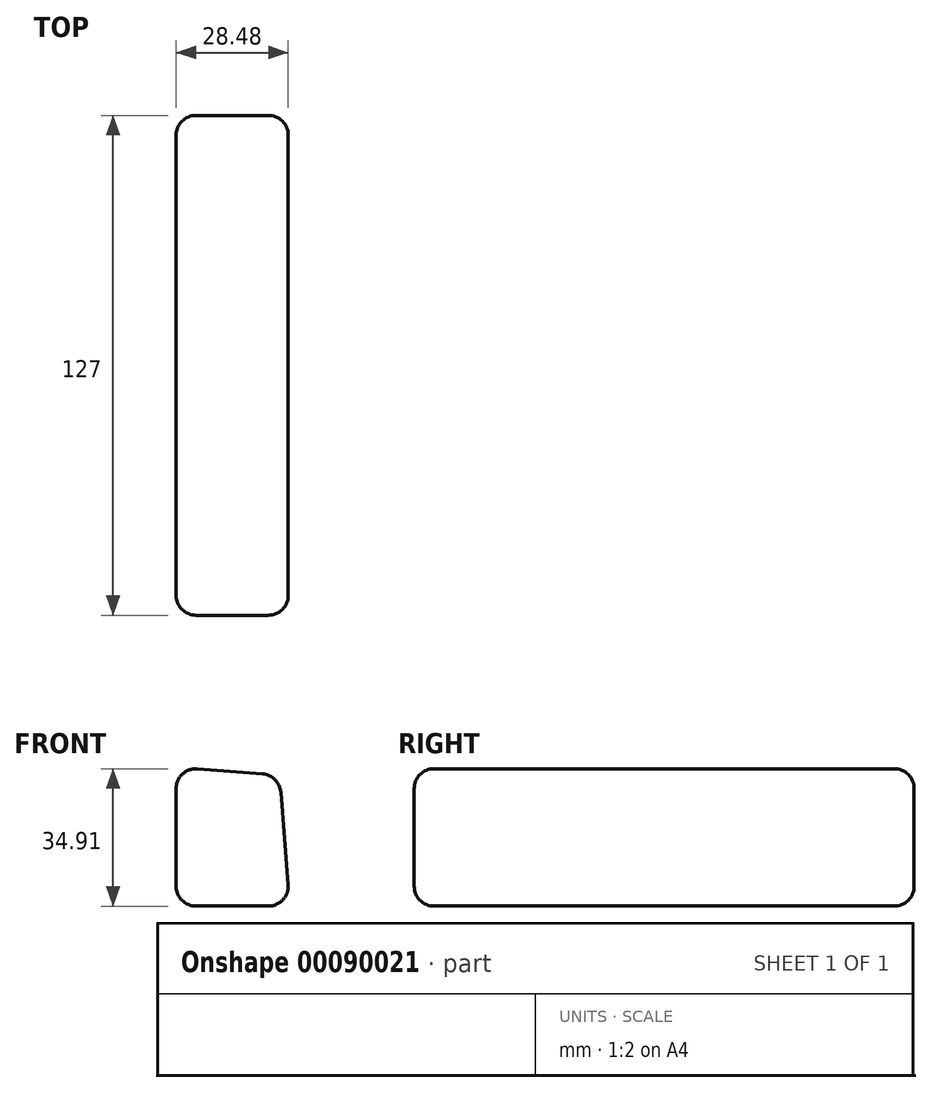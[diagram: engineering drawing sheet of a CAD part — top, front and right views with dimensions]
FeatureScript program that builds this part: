
annotation { "Feature Type Name" : "Feature", "Feature Type Description" : "" }
export const myFeature = defineFeature(function(context is Context, id is Id, definition is map)
    precondition{}
    {
        {
            var Q0;
            Q0=qCreatedBy(makeId("Front.planeOp"),FACE);
            var sketch = newSketch(context, id + "F0", { "sketchPlane" : qUnion([Q0])});
            skLineSegment(sketch, "E0", {"start": v(-57.24, 44.5) * mm, "end": v(-57.24, 9.16) * mm});
            skLineSegment(sketch, "E1", {"start": v(-57.24, 9.16) * mm, "end": v(-28.34, 9.16) * mm});
            skLineSegment(sketch, "E2", {"start": v(-28.34, 9.16) * mm, "end": v(-30.98, 42.41) * mm});
            skLineSegment(sketch, "E3", {"start": v(-57.24, 44.5) * mm, "end": v(-30.98, 42.41) * mm});
            skSolve(sketch);
        }
        {
            var Q0;
            Q0=qSketchRegion(id+"F0",true);
            extrude(context, id + "F1", {"entities" : qUnion([Q0]), "depth" : 127 * mm});
        }
        {
            var Q0;
            Q0=makeQuery(id+"F1.opExtrude","SWEPT_EDGE",EDGE,{"disambiguationData":[OSD([sQuery(id+"F0.wireOp",EDGE,"E2"),sQuery(id+"F0.wireOp",EDGE,"E3")])]});
            var Q1;
            Q1=makeQuery(id+"F1.opExtrude","SWEPT_EDGE",EDGE,{"disambiguationData":[OSD([sQuery(id+"F0.wireOp",EDGE,"E0"),sQuery(id+"F0.wireOp",EDGE,"E3")])]});
            var Q2;
            Q2=makeQuery(id+"F1.opExtrude","CAP_EDGE",EDGE,{"disambiguationData":[OSD([sQuery(id+"F0.wireOp",EDGE,"E3")])],"isStart":false});
            var Q3;
            Q3=makeQuery(id+"F1.opExtrude","CAP_EDGE",EDGE,{"disambiguationData":[OSD([sQuery(id+"F0.wireOp",EDGE,"E2")])],"isStart":false});
            var Q4;
            Q4=makeQuery(id+"F1.opExtrude","CAP_EDGE",EDGE,{"disambiguationData":[OSD([sQuery(id+"F0.wireOp",EDGE,"E1")])],"isStart":false});
            var Q5;
            Q5=makeQuery(id+"F1.opExtrude","CAP_EDGE",EDGE,{"disambiguationData":[OSD([sQuery(id+"F0.wireOp",EDGE,"E0")])],"isStart":false});
            var Q6;
            Q6=makeQuery(id+"F1.opExtrude","SWEPT_EDGE",EDGE,{"disambiguationData":[OSD([sQuery(id+"F0.wireOp",EDGE,"E1"),sQuery(id+"F0.wireOp",EDGE,"E2")])]});
            var Q7;
            Q7=makeQuery(id+"F1.opExtrude","SWEPT_EDGE",EDGE,{"disambiguationData":[OSD([sQuery(id+"F0.wireOp",EDGE,"E0"),sQuery(id+"F0.wireOp",EDGE,"E1")])]});
            var Q8;
            Q8=makeQuery(id+"F1.opExtrude","CAP_EDGE",EDGE,{"disambiguationData":[OSD([sQuery(id+"F0.wireOp",EDGE,"E2")])],"isStart":true});
            var Q9;
            Q9=makeQuery(id+"F1.opExtrude","CAP_EDGE",EDGE,{"disambiguationData":[OSD([sQuery(id+"F0.wireOp",EDGE,"E3")])],"isStart":true});
            var Q10;
            Q10=makeQuery(id+"F1.opExtrude","CAP_EDGE",EDGE,{"disambiguationData":[OSD([sQuery(id+"F0.wireOp",EDGE,"E0")])],"isStart":true});
            var Q11;
            Q11=makeQuery(id+"F1.opExtrude","CAP_EDGE",EDGE,{"disambiguationData":[OSD([sQuery(id+"F0.wireOp",EDGE,"E1")])],"isStart":true});
            fillet(context, id + "F2", {"entities" : qUnion([Q0, Q1, Q2, Q3, Q4, Q5, Q6, Q7, Q8, Q9, Q10, Q11]), "radius" : 5.08 * mm, "tangentPropagation" : true, "allowEdgeOverflow" : false});
        }
    });
